# Revit family: Arctic Boiler 3500-6000
name_source: partatom
category: Mechanical Equipment
revit_build: Autodesk Revit 2018 (Build: 20170223_1515(x64)
units: mm (PartAtom-declared; Revit-internal decimal feet)

## family parameters
Always vertical = Yes
Cut with Voids When Loaded = No
OmniClass Number = 23.75.00.00
OmniClass Title = Climate Control (HVAC)
Part Type = Normal
Room Calculation Point = No
Round Connector Dimension = Use Diameter
Shared = No
Work Plane-Based = No

## types (2) — shared parameters
Boiler Drain = 1" NPT
Condensate Drain = 1" NPT
Electrical Knockouts = 3/4" Conduit
Gas Train = 2" NPT
Height = 81"
Hydronic Return = 6" Pipe Flange Class 150
Hydronic Supply = 6" Pipe Flange Class 150
Manufacturer = Bryan Steam
Width = 63 1/4"

## per-type parameters (varying)
| type | Air Supply | Air Supply Angle Ring Dia. | Air Supply Dia. | Air Supply Location From Front | Air Supply Location From Left Side | Gas Train Location | Hydronic Return Location | Hydronic Supply Location | Length | Stack Dia. | Stack Location | Vent |
| ARC4000 | 12" | 12 3/8" | 12" | 8 5/8" | 8 5/8" | 24 1/8" | 11 3/8" | 18 5/8" | 84" | 12" | 10 3/8" | 12" EZ Vent |
| ARC6000 | 14" | 14 3/8" | 14" | 9 5/8" | 9 5/8" | 27 7/8" | 15 1/8" | 22 3/8" | 102" | 14" | 11 3/8" | 14" EZ Vent |

## geometry (parser evidence)
native form markers: Sweep x2
no freeform markers — native parametric forms only
